# Revit family: Univers-IP30-leer-Unterputz-AT-de
name_source: partatom
category: Electrical Equipment
units: mm (PartAtom-declared; Revit-internal decimal feet)

## family parameters
Cut with Voids When Loaded = No
Host = Face
Panel Configuration = Two Columns, Circuits Across
Part Type = Panelboard
Room Calculation Point = No
Round Connector Dimension = Use Diameter
Shared = No

## types (20) — shared parameters
EF000003 - Montageart = EV001247 - Aufputz/Unterputz
EF000007 - Farbe = EV000202 - weiß
EF000116 - RAL-Nummer = 9010
EF000339 - Art der Abdeckung = EV000494 - ohne
EF001062 - EMV-Ausführung = No
EF001088 - Anbaumöglichkeit = No
EF001134 - DIN-Schiene = No
EF001596 - Werkstoff des Gehäuses = EV000179 - Stahl
EF004462 - Art der Schließung = EV000154 - sonstige
EF005474 - Schutzart (IP) = EV006410 - IP30
EF006244 - Transparenter Deckel/Tür = No
EF006306 - Mit Schloss = No
EF009212 - Ausführung Deckel = EV009916 - mit Ausschnitt
EF015776 - Erdungsklemmenblock = No
EF015777 - Neutralleiterklemmenblock = No
EF015941 - Signaldurchlassende Tür = No
HG000002 - Mit tür = No
HG000003 - Bereich = Univers
HG000005 - Dicke = 3 mm  [stored 0.00984252 ft]
HG000006 - Unterputz = Yes
HG000009 - Doppelflügeligen Tür = No
HG000010 - Asymmetrische Türen = No
HG000011 - Leere Reihen von unten = No
Manufacturer = Hager
Type Comments = Univers
zero-valued in all types: Default Elevation, EF000266 - Anzahl der Reihen, EF002950 - Breite in Teilungseinheiten, HG000001 - Anzahl der Spalten, HG000007 - Anzahl der leeren Spalten, HG000008 - Anzahl der leeren Reihen

## per-type parameters (varying)
| type | EF000008 - Breite | EF000040 - Höhe | EF000049 - Tiefe | EF000118 - Mit Montageplatte | EF000218 - Einbautiefe | EF000332 - Einbauhöhe | EF000846 - Einbaubreite | EF001131 - Innentiefe | HG000004 - Herstellerreferenz | Model |
| Unterputz IP30 B1050 H1100 T161 0 Teilungseinheiten - FWQ74D1 | 1050 mm | 1100 mm | 161 mm  [stored 0.528215 ft] | Yes | 161 mm  [stored 0.528215 ft] | 1100 mm | 1050 mm | 161 mm  [stored 0.528215 ft] | FWQ74D1 | FWQ74D1 |
| Unterputz IP30 B1050 H650 T160 0 Teilungseinheiten - FWQ34D1 | 1050 mm | 650 mm  [stored 2.13255 ft] | 160 mm  [stored 0.524934 ft] | Yes | 160 mm  [stored 0.524934 ft] | 650 mm  [stored 2.13255 ft] | 1050 mm | 160 mm  [stored 0.524934 ft] | FWQ34D1 | FWQ34D1 |
| Unterputz IP30 B1050 H650 T160 0 Teilungseinheiten - FWQ44D1 | 1050 mm | 650 mm  [stored 2.13255 ft] | 160 mm  [stored 0.524934 ft] | Yes | 160 mm  [stored 0.524934 ft] | 650 mm  [stored 2.13255 ft] | 1050 mm | 160 mm  [stored 0.524934 ft] | FWQ44D1 | FWQ44D1 |
| Unterputz IP30 B1050 H800 T160 0 Teilungseinheiten - FWQ54D1 | 1050 mm | 800 mm  [stored 2.62467 ft] | 160 mm  [stored 0.524934 ft] | Yes | 160 mm  [stored 0.524934 ft] | 800 mm  [stored 2.62467 ft] | 1050 mm | 160 mm  [stored 0.524934 ft] | FWQ54D1 | FWQ54D1 |
| Unterputz IP30 B1050 H950 T160 0 Teilungseinheiten - FWQ64D1 | 1050 mm | 950 mm  [stored 3.1168 ft] | 160 mm  [stored 0.524934 ft] | Yes | 160 mm  [stored 0.524934 ft] | 950 mm  [stored 3.1168 ft] | 1050 mm | 160 mm  [stored 0.524934 ft] | FWQ64D1 | FWQ64D1 |
| Unterputz IP30 B300 H1100 T160 0 Teilungseinheiten - FWQ71D1 | 300 mm | 1100 mm | 160 mm  [stored 0.524934 ft] | Yes | 160 mm  [stored 0.524934 ft] | 1100 mm | 300 mm | 160 mm  [stored 0.524934 ft] | FWQ71D1 | FWQ71D1 |
| Unterputz IP30 B300 H500 T160 0 Teilungseinheiten - FWQ31D1 | 300 mm | 500 mm  [stored 1.64042 ft] | 160 mm  [stored 0.524934 ft] | Yes | 160 mm  [stored 0.524934 ft] | 500 mm  [stored 1.64042 ft] | 300 mm | 160 mm  [stored 0.524934 ft] | FWQ31D1 | FWQ31D1 |
| Unterputz IP30 B300 H650 T160 0 Teilungseinheiten - FWQ41D1 | 300 mm | 650 mm  [stored 2.13255 ft] | 160 mm  [stored 0.524934 ft] | Yes | 160 mm  [stored 0.524934 ft] | 650 mm  [stored 2.13255 ft] | 300 mm | 160 mm  [stored 0.524934 ft] | FWQ41D1 | FWQ41D1 |
| Unterputz IP30 B300 H800 T160 0 Teilungseinheiten - FWQ51D1 | 300 mm | 800 mm  [stored 2.62467 ft] | 160 mm  [stored 0.524934 ft] | Yes | 160 mm  [stored 0.524934 ft] | 800 mm  [stored 2.62467 ft] | 300 mm | 160 mm  [stored 0.524934 ft] | FWQ51D1 | FWQ51D1 |
| Unterputz IP30 B300 H950 T160 0 Teilungseinheiten - FWQ61D1 | 300 mm | 950 mm  [stored 3.1168 ft] | 160 mm  [stored 0.524934 ft] | Yes | 160 mm  [stored 0.524934 ft] | 950 mm  [stored 3.1168 ft] | 300 mm | 160 mm  [stored 0.524934 ft] | FWQ61D1 | FWQ61D1 |
| Unterputz IP30 B550 H1100 T160 0 Teilungseinheiten - FWQ72D1 | 550 mm | 1100 mm | 160 mm  [stored 0.524934 ft] | Yes | 160 mm  [stored 0.524934 ft] | 1100 mm | 550 mm | 160 mm  [stored 0.524934 ft] | FWQ72D1 | FWQ72D1 |
| Unterputz IP30 B550 H500 T160 0 Teilungseinheiten - FWQ32D1 | 550 mm | 500 mm  [stored 1.64042 ft] | 160 mm  [stored 0.524934 ft] | Yes | 160 mm  [stored 0.524934 ft] | 500 mm  [stored 1.64042 ft] | 550 mm | 160 mm  [stored 0.524934 ft] | FWQ32D1 | FWQ32D1 |
| Unterputz IP30 B550 H650 T160 0 Teilungseinheiten - FWQ42D1 | 550 mm | 650 mm  [stored 2.13255 ft] | 160 mm  [stored 0.524934 ft] | Yes | 160 mm  [stored 0.524934 ft] | 650 mm  [stored 2.13255 ft] | 550 mm | 160 mm  [stored 0.524934 ft] | FWQ42D1 | FWQ42D1 |
| Unterputz IP30 B550 H800 T160 0 Teilungseinheiten - FWQ52D1 | 550 mm | 800 mm  [stored 2.62467 ft] | 160 mm  [stored 0.524934 ft] | Yes | 160 mm  [stored 0.524934 ft] | 800 mm  [stored 2.62467 ft] | 550 mm | 160 mm  [stored 0.524934 ft] | FWQ52D1 | FWQ52D1 |
| Unterputz IP30 B550 H950 T160 0 Teilungseinheiten - FWQ62D1 | 550 mm | 950 mm  [stored 3.1168 ft] | 160 mm  [stored 0.524934 ft] | Yes | 160 mm  [stored 0.524934 ft] | 950 mm  [stored 3.1168 ft] | 550 mm | 160 mm  [stored 0.524934 ft] | FWQ62D1 | FWQ62D1 |
| Unterputz IP30 B800 H1100 T161 0 Teilungseinheiten - FWQ73D1 | 800 mm  [stored 2.62467 ft] | 1100 mm | 161 mm  [stored 0.528215 ft] | Yes | 161 mm  [stored 0.528215 ft] | 1100 mm | 800 mm  [stored 2.62467 ft] | 161 mm  [stored 0.528215 ft] | FWQ73D1 | FWQ73D1 |
| Unterputz IP30 B800 H500 T160 0 Teilungseinheiten - FWQ33D1 | 800 mm  [stored 2.62467 ft] | 500 mm  [stored 1.64042 ft] | 160 mm  [stored 0.524934 ft] | No | 160 mm  [stored 0.524934 ft] | 500 mm  [stored 1.64042 ft] | 800 mm  [stored 2.62467 ft] | 156 mm  [stored 0.511811 ft] | FWQ33D1 | FWQ33D1 |
| Unterputz IP30 B800 H650 T160 0 Teilungseinheiten - FWQ43D1 | 800 mm  [stored 2.62467 ft] | 650 mm  [stored 2.13255 ft] | 160 mm  [stored 0.524934 ft] | Yes | 160 mm  [stored 0.524934 ft] | 650 mm  [stored 2.13255 ft] | 800 mm  [stored 2.62467 ft] | 160 mm  [stored 0.524934 ft] | FWQ43D1 | FWQ43D1 |
| Unterputz IP30 B800 H800 T160 0 Teilungseinheiten - FWQ53D1 | 800 mm  [stored 2.62467 ft] | 800 mm  [stored 2.62467 ft] | 160 mm  [stored 0.524934 ft] | Yes | 160 mm  [stored 0.524934 ft] | 800 mm  [stored 2.62467 ft] | 800 mm  [stored 2.62467 ft] | 160 mm  [stored 0.524934 ft] | FWQ53D1 | FWQ53D1 |
| Unterputz IP30 B800 H950 T160 0 Teilungseinheiten - FWQ63D1 | 800 mm  [stored 2.62467 ft] | 950 mm  [stored 3.1168 ft] | 160 mm  [stored 0.524934 ft] | Yes | 160 mm  [stored 0.524934 ft] | 950 mm  [stored 3.1168 ft] | 800 mm  [stored 2.62467 ft] | 160 mm  [stored 0.524934 ft] | FWQ63D1 | FWQ63D1 |

note: [stored X ft] marks values corroborated as IEEE doubles in the binary element streams (Revit-internal decimal feet)

## geometry (parser evidence)
native form markers: Sweep x12
no freeform markers — native parametric forms only
